# Revit family: Server Rack v1.3.ex
name_source: partatom
category: Electrical Fixtures
revit_build: Autodesk Revit 2013 (Build: 20121003_2115(x64)
units: mm (PartAtom-declared; Revit-internal decimal feet)

## types (7) — shared parameters
ActualAirTemperatureDifference = 0 °F
ActualExhaustAirTemperature = 0 °F
ActualExhaustAirflow = 0 CFM
ActualSupplyAirTemperature = 0 °F
ActualSupplyAirflow = 0 CFM
CompatiblePower = 0 kW
DesignAirTemperatureDifference = 0 °F
DesignExhaustAirTemperature = 0 °F
DesignExhaustAirflow = 0 CFM
DesignPrimaryCurrent = 0 A
DesignSupplyAirTemperature = 0 °F
DesignSupplyAirflow = 0 CFM
ElectricalConnectorHeight = 75"
EquipmentType = Server Rack
LoadClassification = Power
Manufacturer = -
MaxEquipmentTotalPower = 0 kW
Model = -
OperatingWeight = 0.00 lb
PrimaryPhases = 3
UnitHeight = 82 3/4"
zero-valued in all types: CircuitBreakerQuantity, Cost, PowerStripQuantity, RackSwitchQuantity, UplinkQuantity

## per-type parameters (varying)
| type | AnnotationVisible | CabinetType | ClusterNumber | ClusterType | DesignPrimaryTotalPower | DesignPrimaryVoltage | DesignSecondaryVoltage | Designation | GhostedGeometryVisible | Licensing | RackSize | RackType | RackYear | SecondaryPhases | ServerRackGeometryVisible | TripletInnerLinesDistance | TripletInternalLinesVisible | UPSType | UnitDepth | UnitWidth |
| A | Yes |  | 6 | FE | 10.8 kW | 277 V | 48 V | A | No |  | Singlet | I-web-f | 2013 | 1 | Yes | 8" | No |  | 42" | 24" |
| _Ghost Triplet | Yes | - | - | - | 0 kW | 277 V | 48 V | GH | Yes |  |  | Triplet | 0 | 3 | No | 22 21/32" | No |  | 36" | 68" |
| _Blank | No |  | - | - | 0 kW | 480 V | 0 V | BL | No |  |  | Blizzank | 0 | 3 | No | 8" | No |  | 42" | 24" |
| _Triplet | Yes |  | - | - | 0 kW | 480 V | 0 V | - | No |  |  | Triplet | 0 | 3 | Yes | 22 21/32" | Yes |  | 36" | 68" |
| _Singlet | Yes |  | - | - | 0 kW | 277 V | 48 V | - | No |  |  | Singlet | 0 | 1 | Yes | 8" | No |  | 42" | 24" |
| _Ghost Singlet | Yes | - | - | - | 0 kW | 277 V | 48 V | GH | Yes | http://tlcircle3d.blogspot.com |  | Singlet | 0 | 3 | No | 8" | No |  | 42" | 24" |
| U | Yes |  | 8 | DEV | 20 kW | 480 V | 0 V | U | No |  | Triplet | VI-feed-f-dc | 2012 | 3 | Yes | 22 21/32" | Yes | DCUPS | 36" | 68" |

## geometry (parser evidence)
native form markers: Sweep x2
no freeform markers — native parametric forms only
